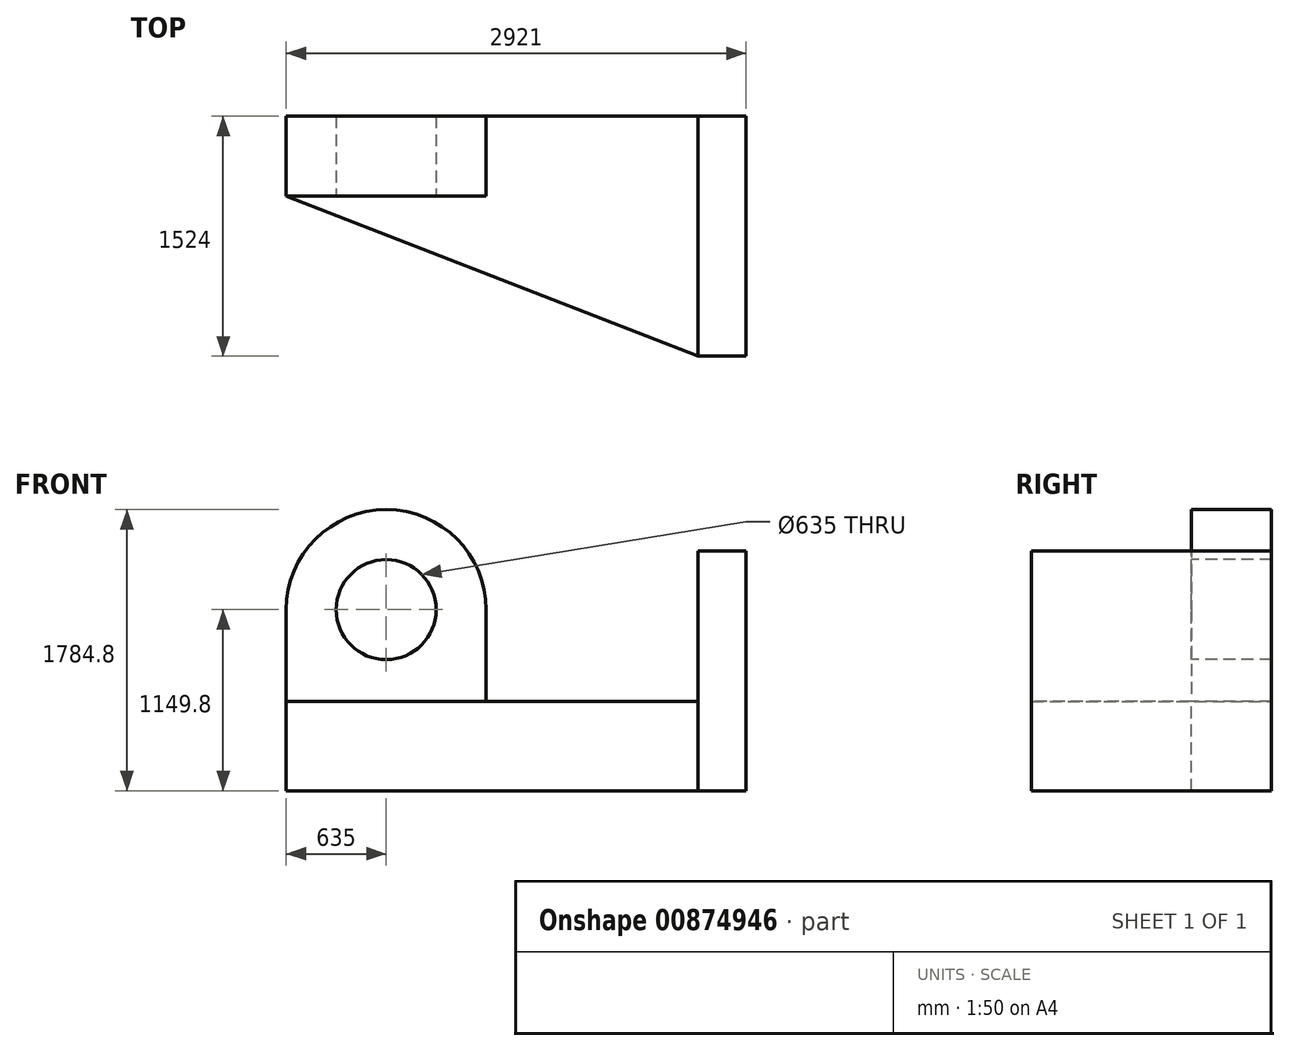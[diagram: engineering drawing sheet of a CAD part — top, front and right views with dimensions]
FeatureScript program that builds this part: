
annotation { "Feature Type Name" : "Feature", "Feature Type Description" : "" }
export const myFeature = defineFeature(function(context is Context, id is Id, definition is map)
    precondition{}
    {
        {
            var Q0;
            Q0=qCreatedBy(makeId("Right.planeOp"),FACE);
            var sketch = newSketch(context, id + "F0", { "sketchPlane" : qUnion([Q0])});
            skLineSegment(sketch, "E0.bottom", {"start": v(0, 0) * mm, "end": v(-1524, 0) * mm});
            skLineSegment(sketch, "E0.top", {"start": v(0, 1524) * mm, "end": v(-1524, 1524) * mm});
            skLineSegment(sketch, "E0.left", {"start": v(0, 0) * mm, "end": v(0, 1524) * mm});
            skLineSegment(sketch, "E0.right", {"start": v(-1524, 0) * mm, "end": v(-1524, 1524) * mm});
            skSolve(sketch);
        }
        {
            var Q0;
            Q0=makeQuery(id+"F0.imprint","IMPRINT",FACE,{"disambiguationData":[TD([[makeQuery(id+"F0.imprint","IMPRINT",EDGE,{"derivedFrom":sQuery(id+"F0.wireOp",EDGE,"E0.bottom")}),-1.0]])]});
            extrude(context, id + "F1", {"entities" : qUnion([Q0]), "depth" : 304.8 * mm, "offsetDistance" : 25.4 * mm});
        }
        {
            var Q0;
            Q0=makeQuery(id+"F1.opExtrude","CAP_FACE",FACE,{"disambiguationData":[OSD([sQuery(id+"F0.wireOp",EDGE,"E0.bottom"),sQuery(id+"F0.wireOp",EDGE,"E0.top"),sQuery(id+"F0.wireOp",EDGE,"E0.left"),sQuery(id+"F0.wireOp",EDGE,"E0.right")])],"isStart":false});
            var sketch = newSketch(context, id + "F2", { "sketchPlane" : qUnion([Q0])});
            skLineSegment(sketch, "E1.bottom", {"start": v(-1524, 0) * mm, "end": v(0, 0) * mm});
            skLineSegment(sketch, "E1.top", {"start": v(-1524, 565.6) * mm, "end": v(0, 565.6) * mm});
            skLineSegment(sketch, "E1.left", {"start": v(-1524, 0) * mm, "end": v(-1524, 565.6) * mm});
            skLineSegment(sketch, "E1.right", {"start": v(0, 0) * mm, "end": v(0, 565.6) * mm});
            skSolve(sketch);
        }
        {
            var Q0;
            Q0=makeQuery(id+"F2.imprint","IMPRINT",FACE,{"disambiguationData":[TD([[makeQuery(id+"F2.imprint","IMPRINT",EDGE,{"derivedFrom":sQuery(id+"F2.wireOp",EDGE,"E1.bottom")}),-1.0]])]});
            extrude(context, id + "F3", {"entities" : qUnion([Q0]), "operationType" : NewBodyOperationType.ADD, "oppositeDirection" : true, "depth" : 2921 * mm, "offsetDistance" : 25.4 * mm});
        }
        {
            var Q0;
            Q0=makeQuery(id+"F3.opExtrude","SWEPT_FACE",FACE,{"disambiguationData":[OSD([sQuery(id+"F2.wireOp",EDGE,"E1.top")])]});
            var sketch = newSketch(context, id + "F4", { "sketchPlane" : qUnion([Q0])});
            skLineSegment(sketch, "E2.bottom", {"start": v(-2616.2, 0) * mm, "end": v(-1346.2, 0) * mm});
            skLineSegment(sketch, "E2.top", {"start": v(-2616.2, -508) * mm, "end": v(-1346.2, -508) * mm});
            skLineSegment(sketch, "E2.left", {"start": v(-2616.2, 0) * mm, "end": v(-2616.2, -508) * mm});
            skLineSegment(sketch, "E2.right", {"start": v(-1346.2, 0) * mm, "end": v(-1346.2, -508) * mm});
            skSolve(sketch);
        }
        {
            var Q0;
            Q0 = qSketchRegion(id + "F4", true);
            extrude(context, id + "F5", {"entities" : qUnion([Q0]), "operationType" : NewBodyOperationType.ADD, "depth" : 584.2 * mm, "offsetDistance" : 25.4 * mm});
        }
        {
            var Q0;
            Q0=makeQuery(id+"F5.opExtrude","SWEPT_FACE",FACE,{"disambiguationData":[OSD([sQuery(id+"F4.wireOp",EDGE,"E2.top")])]});
            var sketch = newSketch(context, id + "F6", { "sketchPlane" : qUnion([Q0])});
            skCircle(sketch, "E3", {"center": v(-1981.2, 1149.8) * mm, "radius": 635 * mm});
            skSolve(sketch);
        }
        {
            var Q0;
            {var subQ1=sQuery(id+"F4.wireOp",EDGE,"E2.top");var subQ2=makeQuery(id+"F5.opExtrude","CAP_EDGE",EDGE,{"disambiguationData":[OSD([subQ1])],"isStart":false});Q0=makeQuery(id+"F6.imprint","IMPRINT",FACE,{"disambiguationData":[TD([[makeQuery(id+"F6.imprint","IMPRINT",EDGE,{"derivedFrom":subQ2}),1.0]])]});}
            extrude(context, id + "F7", {"entities" : qUnion([Q0]), "operationType" : NewBodyOperationType.ADD, "oppositeDirection" : true, "depth" : 508 * mm, "offsetDistance" : 25.4 * mm});
        }
        {
            var Q0;
            {var subQ0=sQuery(id+"F4.wireOp",EDGE,"E2.top");Q0=makeQuery(id+"F7.boolean.opBoolean","MERGE",FACE,{"derivedFrom":[makeQuery(id+"F5.opExtrude","SWEPT_FACE",FACE,{"disambiguationData":[OSD([subQ0])]}),makeQuery(id+"F7.opExtrude","CAP_FACE",FACE,{"disambiguationData":[OSD([subQ0,sQuery(id+"F6.wireOp",EDGE,"E3")])],"isStart":true})]});}
            var sketch = newSketch(context, id + "F8", { "sketchPlane" : qUnion([Q0])});
            skCircle(sketch, "E4", {"center": v(-1981.2, 1149.8) * mm, "radius": 317.5 * mm});
            skSolve(sketch);
        }
        {
            var Q0;
            Q0=makeQuery(id+"F8.imprint","IMPRINT",FACE,{"disambiguationData":[TD([[makeQuery(id+"F8.imprint","IMPRINT",EDGE,{"derivedFrom":sQuery(id+"F8.wireOp",EDGE,"E4")}),1.0]])]});
            extrude(context, id + "F9", {"entities" : qUnion([Q0]), "operationType" : NewBodyOperationType.REMOVE, "oppositeDirection" : true, "depth" : 25.4 * mm, "offsetDistance" : 25.4 * mm});
        }
        {
            var Q0;
            Q0=makeQuery(id+"F9.boolean.opBoolean","COPY",FACE,{"derivedFrom":makeQuery(id+"F9.opExtrude","CAP_FACE",FACE,{"disambiguationData":[OSD([sQuery(id+"F8.wireOp",EDGE,"E4")])],"isStart":false})});
            extrude(context, id + "F10", {"entities" : qUnion([Q0]), "operationType" : NewBodyOperationType.ADD, "oppositeDirection" : true, "depth" : 25.4 * mm, "offsetDistance" : 25.4 * mm});
        }
        {
            var Q0;
            Q0=makeQuery(id+"F9.boolean.opBoolean","COPY",FACE,{"derivedFrom":makeQuery(id+"F9.opExtrude","CAP_FACE",FACE,{"disambiguationData":[OSD([sQuery(id+"F8.wireOp",EDGE,"E4")])],"isStart":false})});
            var sketch = newSketch(context, id + "F11", { "sketchPlane" : qUnion([Q0])});
            skSolve(sketch);
        }
        {
            var Q0;
            Q0=makeQuery(id+"F11.imprint","IMPRINT",FACE,{"disambiguationData":[TD([[makeQuery(id+"F11.imprint","IMPRINT",EDGE,{"derivedFrom":makeQuery(id+"F9.boolean.opBoolean","COPY",EDGE,{"derivedFrom":makeQuery(id+"F9.opExtrude","CAP_EDGE",EDGE,{"disambiguationData":[OSD([sQuery(id+"F8.wireOp",EDGE,"E4")])],"isStart":false})})}),1.0]])]});
            extrude(context, id + "F12", {"entities" : qUnion([Q0]), "operationType" : NewBodyOperationType.REMOVE, "oppositeDirection" : true, "depth" : 1930.4 * mm, "offsetDistance" : 25.4 * mm});
        }
        {
            var Q0;
            Q0=makeQuery(id+"F3.opExtrude","SWEPT_FACE",FACE,{"disambiguationData":[OSD([sQuery(id+"F2.wireOp",EDGE,"E1.top")])]});
            var sketch = newSketch(context, id + "F13", { "sketchPlane" : qUnion([Q0])});
            skLineSegment(sketch, "E5", {"start": v(-2616.2, -508) * mm, "end": v(0, -1524) * mm});
            skLineSegment(sketch, "E6", {"start": v(0, -1524) * mm, "end": v(-2616.2, -1524) * mm});
            skLineSegment(sketch, "E7", {"start": v(-2616.2, -1524) * mm, "end": v(-2616.2, -508) * mm});
            skSolve(sketch);
        }
        {
            var Q0;
            Q0=makeQuery(id+"F13.imprint","IMPRINT",FACE,{"disambiguationData":[TD([[makeQuery(id+"F13.imprint","IMPRINT",EDGE,{"derivedFrom":sQuery(id+"F13.wireOp",EDGE,"E5")}),-1.0]])]});
            extrude(context, id + "F14", {"entities" : qUnion([Q0]), "operationType" : NewBodyOperationType.REMOVE, "oppositeDirection" : true, "depth" : 2006.6 * mm, "offsetDistance" : 25.4 * mm});
        }
    });
